# Revit family: Lighting_Device-Wireless_Control_Unit-Hubbell_Wiring-WLC
name_source: partatom
category: Lighting Devices
revit_build: Autodesk Revit MEP 2012 (Build: 20110916_2132(x64)
units: mm (PartAtom-declared; Revit-internal decimal feet)

## types (5) — shared parameters
Apparent Load = 6.000 VA
Certifications = FCC, IC Certified
CEC Title 24 Compliant
UL/cUL 916 Listed for Energy Management
Connector Description 1 = Direct Current Power Supply
Connector Description 2 = Alternating Current Power Supply
Connector Description 3 = Controls
DC Voltage = 24 V
Frequency = 60 Hz
Humidity = 0% to 90% non condensing 
relative humidity
Load Classification = Transformer
Manufacturer = Hubbell Wiring Device-Kellems
Number of Poles = 1
Power Factor = 1
Power Factor 2 = 1
Product Documentation Link = http://ecatalog.hubbell-wiring.com
Product Page URL = http://ecatalog.hubbell-wiring.com
URL = http://www.hubbell-wiring.com
zero-valued in all types: Default Elevation

## per-type parameters (varying)
| type | Description | Model | Operating Temperature | Product Material | Type Selector | UPC Number |
| WLC301 | Heavy Duty Control Unit with Integrated Wireless Transmitter | WLCU301 | -40°F (-40 °C) to 149°F(65 °C) | Plastic - Hubbell - Black | WLCU301 | 783585256375 |
| WLC302 | Receives wireless signals and controls its assigned circuits (2) of receptacles ceiling/wall mount sensors | WLC302 | -40°F (-40 °C) to 149°F (65 °C) | Plastic - Hubbell - Black | WLC302 | 783585256184 |
| WLC402W | Furniture Feed Box with Heavy Duty Relays and Integrated Wireless Receiver | WLC402W | 32 °F (0 °C) to 149 °F (65 °C) | Plastic - Hubbell - White | WLC402W | 783585256191 |
| WLCA | Automatic-ON operation, 120/277V AC, 50/60Hz for use with 1 to 4 ATD, ATU and ATP series 
ceiling/wall mount sensors | WLCA | 32°F to 104°F (0°C to 40°C) | Plastic - Hubbell - Black | WLCA |  |
| WLCU301 | Heavy Duty Control Unit with Integrated Wireless Transmitter | WLCU301 | -40°F (-40 °C) to 149°F(65 °C) | Plastic - Hubbell - Black | WLCU301 | 783585256375 |

## geometry (parser evidence)
native form markers: Blend x1, Sweep x11
no freeform markers — native parametric forms only
